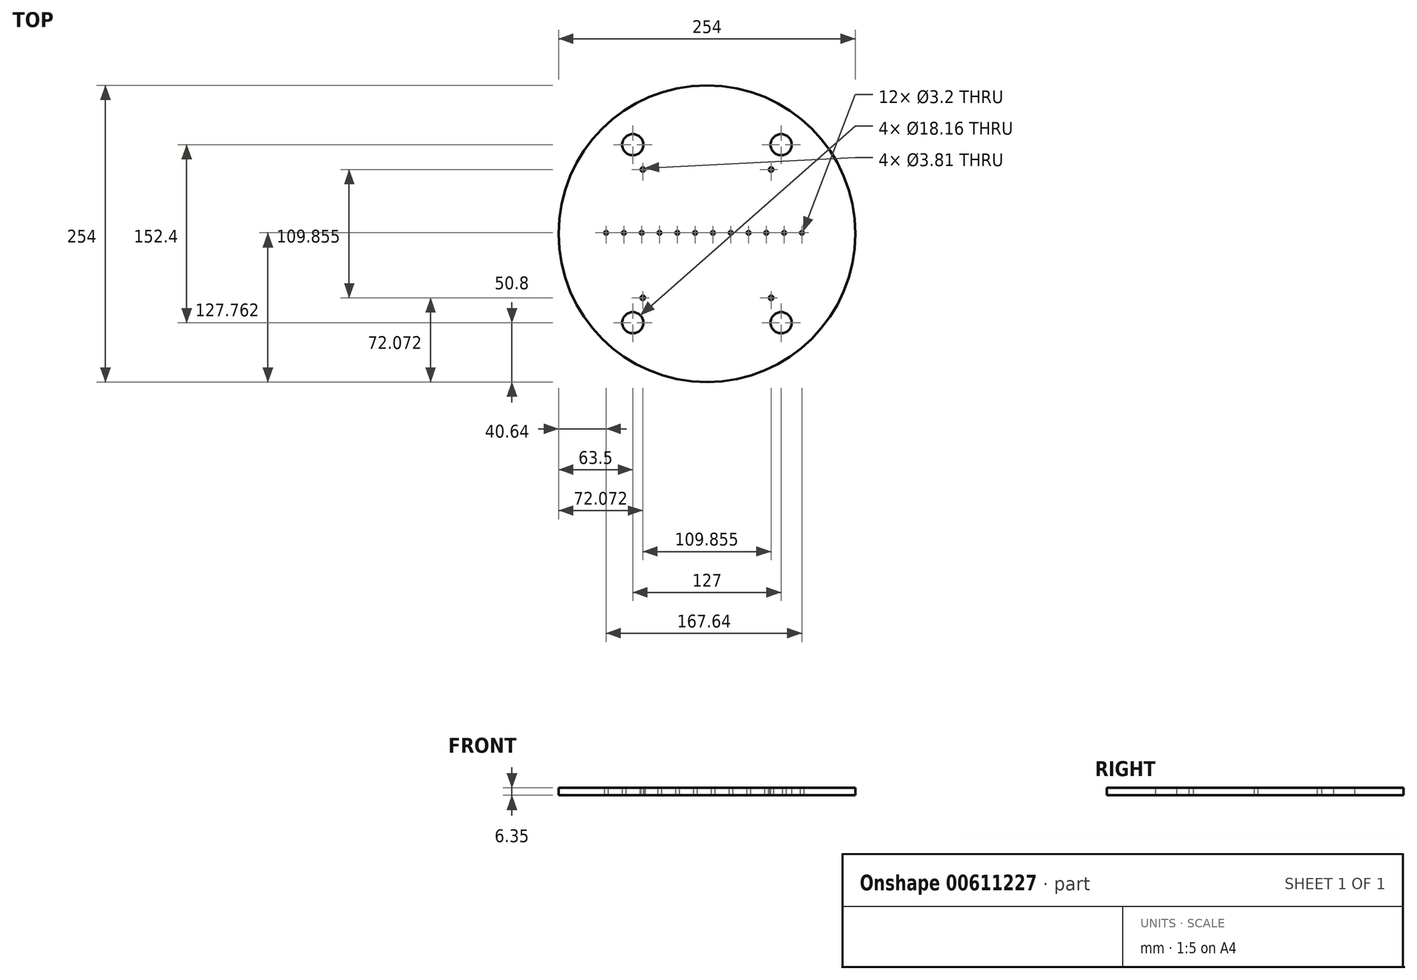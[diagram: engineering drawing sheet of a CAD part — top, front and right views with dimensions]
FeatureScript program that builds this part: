
annotation { "Feature Type Name" : "Feature", "Feature Type Description" : "" }
export const myFeature = defineFeature(function(context is Context, id is Id, definition is map)
    precondition{}
    {
        {
            var Q0;
            Q0=qCreatedBy(makeId("Top.planeOp"),FACE);
            var sketch = newSketch(context, id + "F0", { "sketchPlane" : qUnion([Q0])});
            skCircle(sketch, "E0", {"center": v(-54.93, 54.93) * mm, "radius": 1.9 * mm});
            skCircle(sketch, "E1", {"center": v(54.93, 54.93) * mm, "radius": 1.9 * mm});
            skCircle(sketch, "E2", {"center": v(-54.93, -54.93) * mm, "radius": 1.9 * mm});
            skCircle(sketch, "E3", {"center": v(54.93, -54.93) * mm, "radius": 1.9 * mm});
            skCircle(sketch, "E4", {"center": v(0, 0) * mm, "radius": 127 * mm});
            skCircle(sketch, "E5", {"center": v(-63.5, 76.2) * mm, "radius": 9.08 * mm});
            skCircle(sketch, "E6", {"center": v(63.5, 76.2) * mm, "radius": 9.08 * mm});
            skCircle(sketch, "E7", {"center": v(-63.5, -76.2) * mm, "radius": 9.08 * mm});
            skCircle(sketch, "E8", {"center": v(63.5, -76.2) * mm, "radius": 9.08 * mm});
            skCircle(sketch, "E9", {"center": v(-86.36, 0.76) * mm, "radius": 1.6 * mm});
            skCircle(sketch, "E10.1.0.0", {"center": v(-71.12, 0.76) * mm, "radius": 1.6 * mm});
            skCircle(sketch, "E10.2.0.0", {"center": v(-55.88, 0.76) * mm, "radius": 1.6 * mm});
            skCircle(sketch, "E10.3.0.0", {"center": v(-40.64, 0.76) * mm, "radius": 1.6 * mm});
            skCircle(sketch, "E10.4.0.0", {"center": v(-25.4, 0.76) * mm, "radius": 1.6 * mm});
            skCircle(sketch, "E10.5.0.0", {"center": v(-10.16, 0.76) * mm, "radius": 1.6 * mm});
            skCircle(sketch, "E10.6.0.0", {"center": v(5.08, 0.76) * mm, "radius": 1.6 * mm});
            skCircle(sketch, "E10.7.0.0", {"center": v(20.32, 0.76) * mm, "radius": 1.6 * mm});
            skCircle(sketch, "E10.8.0.0", {"center": v(35.56, 0.76) * mm, "radius": 1.6 * mm});
            skCircle(sketch, "E10.9.0.0", {"center": v(50.8, 0.76) * mm, "radius": 1.6 * mm});
            skCircle(sketch, "E10.10.0.0", {"center": v(66.04, 0.76) * mm, "radius": 1.6 * mm});
            skCircle(sketch, "E10.11.0.0", {"center": v(81.28, 0.76) * mm, "radius": 1.6 * mm});
            skLineSegment(sketch, "E10.direction1", {"start": v(-86.36, 0.76) * mm, "end": v(-71.12, 0.76) * mm, "construction": true});
            skSolve(sketch);
        }
        {
            var Q0;
            Q0=makeQuery(id+"F0.imprint","IMPRINT",FACE,{"disambiguationData":[TD([[makeQuery(id+"F0.imprint","IMPRINT",EDGE,{"derivedFrom":sQuery(id+"F0.wireOp",EDGE,"E0")}),-1.0]])]});
            extrude(context, id + "F1", {"entities" : qUnion([Q0]), "depth" : 6.35 * mm, "offsetDistance" : 25.4 * mm});
        }
    });
